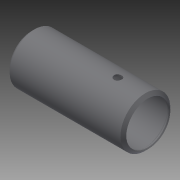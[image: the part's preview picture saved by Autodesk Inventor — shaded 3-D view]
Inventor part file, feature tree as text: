
AUTODESK INVENTOR PART (.ipt)
format: ipt  version: 2014 (Build 180170000, 170)  size: 141,312 bytes
history: native  units: in
note: dims shown in document units (in); Inventor stores cm internally (conversion verified against a paired STEP export)
features: other x56, revolve x2, sketch x2
ambient origin geometry x8: Origin, YZ Plane, XZ Plane, XY Plane, X Axis, Y Axis, Z Axis, Center Point
bodies: Solid1 (feature_tree)
feature tree (60):
  revolve  "Revolution1"  Angle=360.0deg
  revolve  "Revolution2"  [1 undecoded]
  other  "o1_XY"
  other  "o1_YZ"
  other  "o1_ZX"
  other  "o1_X"
  other  "o1_Y"
  other  "o1_Z"
  other  "o1_Center"
  other  "o2_XY"
  other  "o2_YZ"
  other  "o2_ZX"
  other  "o2_X"
  other  "o2_Y"
  other  "o2_Z"
  other  "o2_Center"
  other  "t1_XY"
  other  "t1_YZ"
  other  "t1_ZX"
  other  "t1_X"
  other  "t1_Y"
  other  "t1_Z"
  other  "t1_Center"
  other  "t2_XY"
  other  "t2_YZ"
  other  "t2_ZX"
  other  "t2_X"
  other  "t2_Y"
  other  "t2_Z"
  other  "t2_Center"
  other  "t3_XY"
  other  "t3_YZ"
  other  "t3_ZX"
  other  "t3_X"
  other  "t3_Y"
  other  "t3_Z"
  other  "t3_Center"
  other  "t4_XY"
  other  "t4_YZ"
  other  "t4_ZX"
  other  "t4_X"
  other  "t4_Y"
  other  "t4_Z"
  other  "t4_Center"
  other  "tube1_XY"
  other  "tube1_YZ"
  other  "tube1_ZX"
  other  "tube1_X"
  other  "tube1_Y"
  other  "tube1_Z"
  other  "tube1_Center"
  other  "tube2_XY"
  other  "tube2_YZ"
  other  "tube2_ZX"
  other  "tube2_X"
  other  "tube2_Y"
  other  "tube2_Z"
  other  "tube2_Center"
  sketch  "Sketch_5"
  sketch  "Sketch_1"  dims[d0=360.0deg d1=360.0deg]
note: 1 required parameter value undecoded (feature->parameter linkage not recoverable at this tier; creation-order binding heuristic only, values carry confidence <= 0.55)
